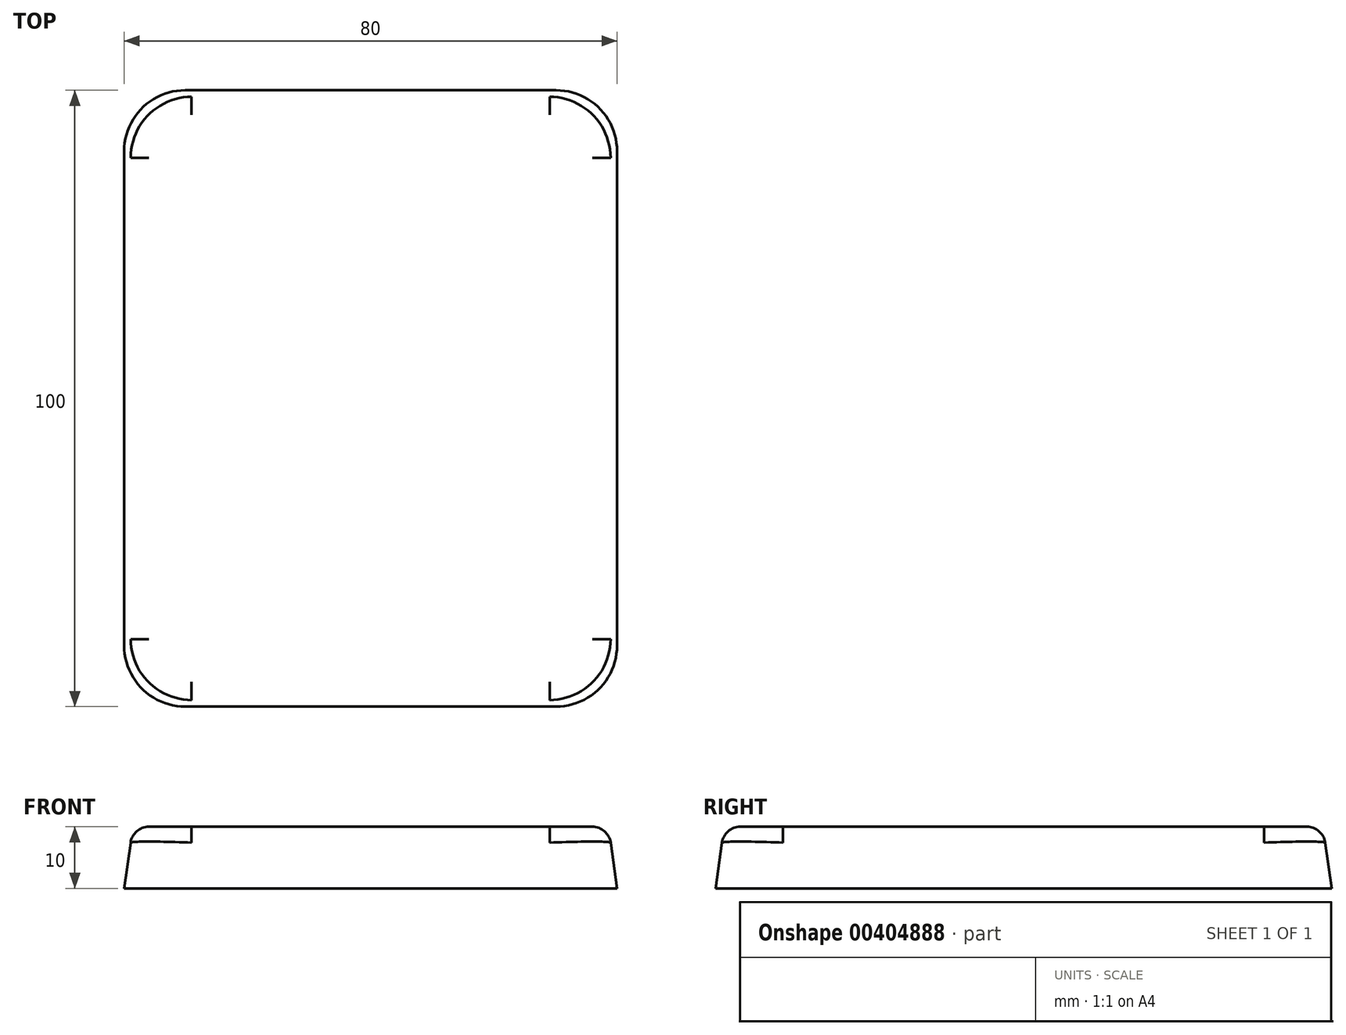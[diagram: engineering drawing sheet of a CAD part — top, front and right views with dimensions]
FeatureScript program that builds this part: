
annotation { "Feature Type Name" : "Feature", "Feature Type Description" : "" }
export const myFeature = defineFeature(function(context is Context, id is Id, definition is map)
    precondition{}
    {
        {
            var Q0;
            Q0=qCreatedBy(makeId("Top.planeOp"),FACE);
            var sketch = newSketch(context, id + "F0", { "sketchPlane" : qUnion([Q0])});
            skLineSegment(sketch, "E0.bottom", {"start": v(40, 50) * mm, "end": v(-40, 50) * mm});
            skLineSegment(sketch, "E0.top", {"start": v(40, -50) * mm, "end": v(-40, -50) * mm});
            skLineSegment(sketch, "E0.left", {"start": v(40, 50) * mm, "end": v(40, -50) * mm});
            skLineSegment(sketch, "E0.right", {"start": v(-40, 50) * mm, "end": v(-40, -50) * mm});
            skPoint(sketch, "E0.middle", {"position": v(0, 0) * mm});
            skSolve(sketch);
        }
        {
            var Q0;
            Q0 = qSketchRegion(id + "F0", true);
            extrude(context, id + "F1", {"entities" : qUnion([Q0]), "depth" : 10 * mm, "hasDraft" : true, "draftAngle" : 8 * degree, "draftPullDirection" : true});
        }
        {
            var Q0;
            Q0=makeQuery(id+"F1.opExtrude","SWEPT_EDGE",EDGE,{"disambiguationData":[OSD([sQuery(id+"F0.wireOp",EDGE,"E0.top"),sQuery(id+"F0.wireOp",EDGE,"E0.right")])]});
            var Q1;
            Q1=makeQuery(id+"F1.opExtrude","SWEPT_EDGE",EDGE,{"disambiguationData":[OSD([sQuery(id+"F0.wireOp",EDGE,"E0.top"),sQuery(id+"F0.wireOp",EDGE,"E0.left")])]});
            var Q2;
            Q2=makeQuery(id+"F1.opExtrude","SWEPT_EDGE",EDGE,{"disambiguationData":[OSD([sQuery(id+"F0.wireOp",EDGE,"E0.bottom"),sQuery(id+"F0.wireOp",EDGE,"E0.left")])]});
            var Q3;
            Q3=makeQuery(id+"F1.opExtrude","SWEPT_EDGE",EDGE,{"disambiguationData":[OSD([sQuery(id+"F0.wireOp",EDGE,"E0.bottom"),sQuery(id+"F0.wireOp",EDGE,"E0.right")])]});
            fillet(context, id + "F2", {"entities" : qUnion([Q0, Q1, Q2, Q3]), "radius" : 10 * mm, "tangentPropagation" : true, "allowEdgeOverflow" : false});
        }
        {
            var Q0;
            Q0=makeQuery(id+"F1.opExtrude","CAP_EDGE",EDGE,{"disambiguationData":[OSD([sQuery(id+"F0.wireOp",EDGE,"E0.right")])],"isStart":false});
            fillet(context, id + "F3", {"entities" : qUnion([Q0]), "radius" : 3 * mm, "tangentPropagation" : true, "allowEdgeOverflow" : false});
        }
    });
